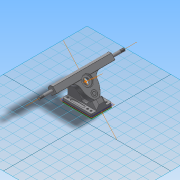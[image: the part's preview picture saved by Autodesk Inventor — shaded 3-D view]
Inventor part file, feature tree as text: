
AUTODESK INVENTOR PART (.ipt)
format: ipt  version: 2014 SP2 (Build 180246200, 246)  size: 483,328 bytes
history: native  units: in
note: dims shown in document units (in); Inventor stores cm internally (conversion verified against a paired STEP export)
features: other x14, sketch x1
ambient origin geometry x8: Origin, YZ Plane, XZ Plane, XY Plane, X Axis, Y Axis, Z Axis, Center Point
bodies: Solid1 (feature_tree), Solid2 (feature_tree), Solid3 (feature_tree)
feature tree (15):
  other  "Truck Caliber50 9in.iam"
  other  "Baseplate Caliber50 9in.ipt:1"
  other  "Hanger Caliber50 9in.ipt:1"
  other  "Generic Riser.ipt:1"
  other  "Axle Centers"
  other  "Parts"
  other  "Work Axis1"
  other  "Work Axis2"
  other  "Work Axis3"
  other  "Vertical Axis"
  other  "Axle Axis"
  other  "Kingpin Axis"
  other  "Work Point1"
  other  "Axle"
  sketch  "Sketch1"  dims[d0=0.3937in d2=3.2677in d3=0.2756in d4=1.9291in d5=4.0625in d9=0.4921in d10=1.5748in d12=360.0deg d14=0.25in d15=0.25in d19=0.1065in d20=0.1065in d21=0.25in d22=0.1065in d23=0.1065in d24=0.25in d25=0.1065in d26=0.1065in d27=0.25in d28=0.1065in d29=0.1065in d30=0.0312in d32=1.378in d34=0.25in d35=0.1065in d36=0.1065in d38=0.25in d40=0.25in d41=0.1065in d42=0.1065in d46=0.5in d47=0.25in d48=0.25in d49=0.1065in d50=0.1065in d51=0.25in d52=0.25in d53=0.25in d54=0.1065in d55=0.1065in d56=0.25in d57=0.25in d58=0.25in d59=0.25in d61=0.25in d64=0.0312in d65=0.25in d66=0.25in d67=0.8in]
